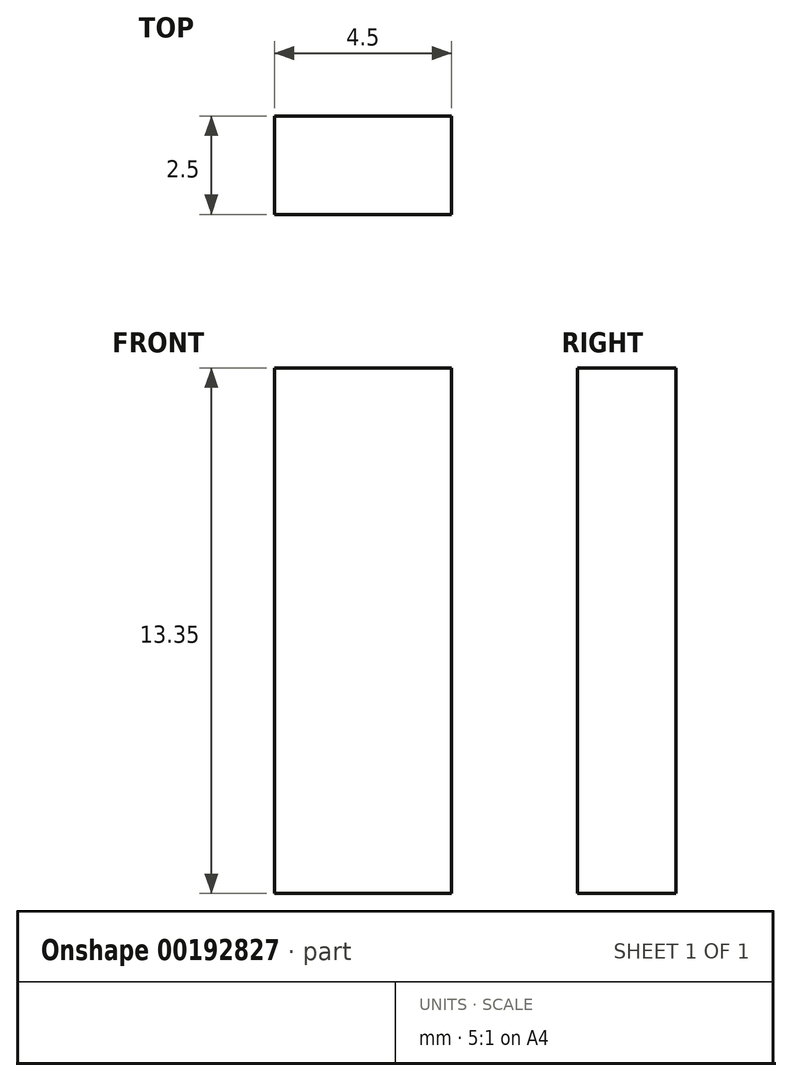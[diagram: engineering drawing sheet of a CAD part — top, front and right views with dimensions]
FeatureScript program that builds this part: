
annotation { "Feature Type Name" : "Feature", "Feature Type Description" : "" }
export const myFeature = defineFeature(function(context is Context, id is Id, definition is map)
    precondition{}
    {
        {
            var Q0;
            Q0=qCreatedBy(makeId("Top.planeOp"),FACE);
            var sketch = newSketch(context, id + "F0", { "sketchPlane" : qUnion([Q0])});
            skLineSegment(sketch, "E0.bottom", {"start": v(-2.25, 1.25) * mm, "end": v(2.25, 1.25) * mm});
            skLineSegment(sketch, "E0.top", {"start": v(-2.25, -1.25) * mm, "end": v(2.25, -1.25) * mm});
            skLineSegment(sketch, "E0.left", {"start": v(-2.25, 1.25) * mm, "end": v(-2.25, -1.25) * mm});
            skLineSegment(sketch, "E0.right", {"start": v(2.25, 1.25) * mm, "end": v(2.25, -1.25) * mm});
            skPoint(sketch, "E0.middle", {"position": v(0, 0) * mm});
            skSolve(sketch);
        }
        {
            var Q0;
            Q0=makeQuery(id+"F0.imprint","IMPRINT",FACE,{"disambiguationData":[TD([[makeQuery(id+"F0.imprint","IMPRINT",EDGE,{"derivedFrom":sQuery(id+"F0.wireOp",EDGE,"E0.bottom")}),-1.0]])]});
            extrude(context, id + "F1", {"entities" : qUnion([Q0]), "depth" : 13.35 * mm});
        }
    });
